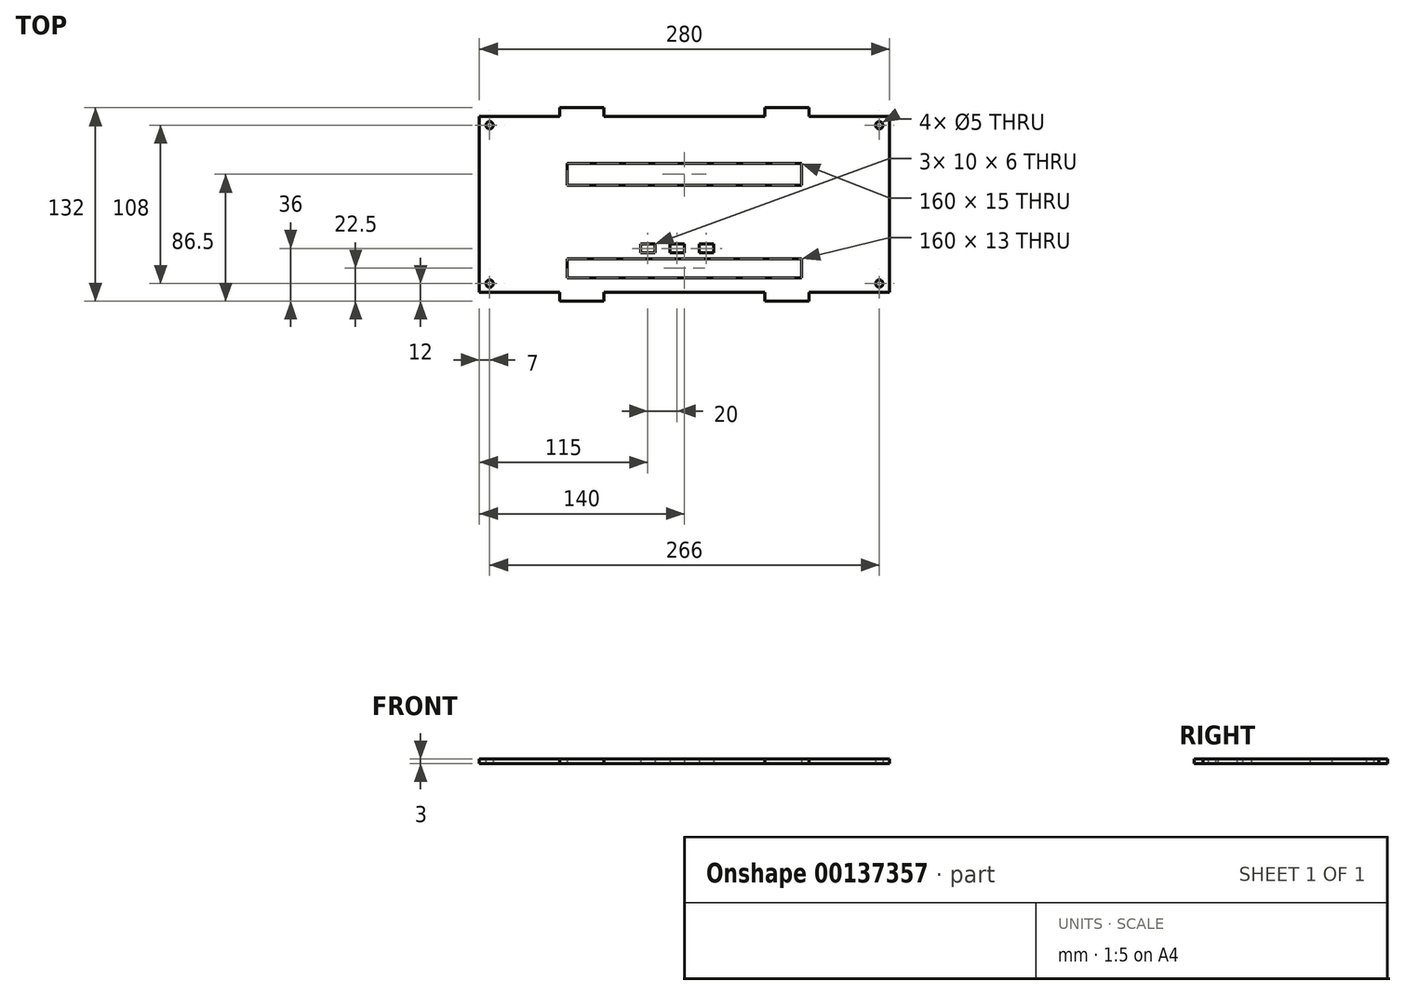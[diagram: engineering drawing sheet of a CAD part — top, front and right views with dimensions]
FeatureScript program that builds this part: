
annotation { "Feature Type Name" : "Feature", "Feature Type Description" : "" }
export const myFeature = defineFeature(function(context is Context, id is Id, definition is map)
    precondition{}
    {
        {
            var Q0;
            Q0=qCreatedBy(makeId("Top.planeOp"),FACE);
            var sketch = newSketch(context, id + "F0", { "sketchPlane" : qUnion([Q0])});
            skLineSegment(sketch, "E0.bottom", {"start": v(140, 60) * mm, "end": v(85, 60) * mm});
            skLineSegment(sketch, "E0.top", {"start": v(140, -60) * mm, "end": v(85, -60) * mm});
            skLineSegment(sketch, "E0.left", {"start": v(140, 60) * mm, "end": v(140, -60) * mm});
            skLineSegment(sketch, "E0.right", {"start": v(-140, 60) * mm, "end": v(-140, -60) * mm});
            skPoint(sketch, "E0.middle", {"position": v(0, 0) * mm});
            skLineSegment(sketch, "E1", {"start": v(-140, -60) * mm, "end": v(-133, -60) * mm, "construction": true});
            skLineSegment(sketch, "E2", {"start": v(-133, -60) * mm, "end": v(-133, -54) * mm, "construction": true});
            skCircle(sketch, "E3", {"center": v(-133, -54) * mm, "radius": 2.5 * mm});
            skCircle(sketch, "E4.MirrorC", {"center": v(-133, 54) * mm, "radius": 2.5 * mm});
            skCircle(sketch, "E5.MirrorC", {"center": v(133, 54) * mm, "radius": 2.5 * mm});
            skCircle(sketch, "E6.MirrorC", {"center": v(133, -54) * mm, "radius": 2.5 * mm});
            skLineSegment(sketch, "E7", {"start": v(0, -50) * mm, "end": v(-80, -50) * mm, "construction": true});
            skLineSegment(sketch, "E8.bottom", {"start": v(-80, -50) * mm, "end": v(80, -50) * mm});
            skLineSegment(sketch, "E8.top", {"start": v(-80, -37) * mm, "end": v(80, -37) * mm});
            skLineSegment(sketch, "E8.left", {"start": v(-80, -50) * mm, "end": v(-80, -37) * mm});
            skLineSegment(sketch, "E8.right", {"start": v(80, -50) * mm, "end": v(80, -37) * mm});
            skLineSegment(sketch, "E9", {"start": v(0, -37) * mm, "end": v(0, -32) * mm, "construction": true});
            skLineSegment(sketch, "E10", {"start": v(0, -32) * mm, "end": v(0, 13) * mm, "construction": true});
            skLineSegment(sketch, "E11", {"start": v(0, 13) * mm, "end": v(0, 28) * mm, "construction": true});
            skLineSegment(sketch, "E12", {"start": v(0, 13) * mm, "end": v(80, 13) * mm});
            skLineSegment(sketch, "E13", {"start": v(80, 13) * mm, "end": v(80, 23) * mm});
            skLineSegment(sketch, "E14", {"start": v(-80, 23) * mm, "end": v(-80, 13) * mm});
            skLineSegment(sketch, "E15", {"start": v(-80, 13) * mm, "end": v(0, 13) * mm});
            skLineSegment(sketch, "E16", {"start": v(0, 28) * mm, "end": v(0, 13) * mm, "construction": true});
            skLineSegment(sketch, "E17", {"start": v(0, 28) * mm, "end": v(0, 26) * mm, "construction": true});
            skLineSegment(sketch, "E18", {"start": v(0, 26) * mm, "end": v(0, 20) * mm, "construction": true});
            skLineSegment(sketch, "E19", {"start": v(0, 20) * mm, "end": v(0, 17) * mm, "construction": true});
            skLineSegment(sketch, "E20", {"start": v(-80, 23) * mm, "end": v(-80, 28) * mm});
            skLineSegment(sketch, "E21", {"start": v(-80, 28) * mm, "end": v(80, 28) * mm});
            skLineSegment(sketch, "E22", {"start": v(80, 28) * mm, "end": v(80, 23) * mm});
            skLineSegment(sketch, "E23", {"start": v(0, 13) * mm, "end": v(0, -27) * mm, "construction": true});
            skLineSegment(sketch, "E24", {"start": v(0, -27) * mm, "end": v(30, -27) * mm, "construction": true});
            skLineSegment(sketch, "E25", {"start": v(0, -27) * mm, "end": v(-30, -27) * mm, "construction": true});
            skLineSegment(sketch, "E26", {"start": v(-30, -27) * mm, "end": v(-30, -33) * mm});
            skLineSegment(sketch, "E27", {"start": v(-30, -33) * mm, "end": v(-20, -33) * mm});
            skLineSegment(sketch, "E28", {"start": v(-20, -33) * mm, "end": v(-20, -27) * mm});
            skLineSegment(sketch, "E29", {"start": v(-30, -27) * mm, "end": v(-20, -27) * mm});
            skLineSegment(sketch, "E30", {"start": v(-20, -27) * mm, "end": v(-10, -27) * mm, "construction": true});
            skLineSegment(sketch, "E31", {"start": v(-10, -27) * mm, "end": v(0, -27) * mm, "construction": true});
            skLineSegment(sketch, "E32", {"start": v(0, -27) * mm, "end": v(10, -27) * mm, "construction": true});
            skLineSegment(sketch, "E33", {"start": v(10, -27) * mm, "end": v(20, -27) * mm, "construction": true});
            skLineSegment(sketch, "E34", {"start": v(20, -27) * mm, "end": v(30, -27) * mm, "construction": true});
            skLineSegment(sketch, "E35", {"start": v(-10, -27) * mm, "end": v(-10, -33) * mm});
            skLineSegment(sketch, "E36", {"start": v(-10, -33) * mm, "end": v(0, -33) * mm});
            skLineSegment(sketch, "E37", {"start": v(0, -33) * mm, "end": v(0, -27) * mm});
            skLineSegment(sketch, "E38", {"start": v(-10, -27) * mm, "end": v(0, -27) * mm});
            skLineSegment(sketch, "E39.bottom", {"start": v(10, -27) * mm, "end": v(20, -27) * mm});
            skLineSegment(sketch, "E39.top", {"start": v(10, -33) * mm, "end": v(20, -33) * mm});
            skLineSegment(sketch, "E39.left", {"start": v(10, -27) * mm, "end": v(10, -33) * mm});
            skLineSegment(sketch, "E39.right", {"start": v(20, -27) * mm, "end": v(20, -33) * mm});
            skLineSegment(sketch, "E40", {"start": v(0, -60) * mm, "end": v(-55, -60) * mm, "construction": true});
            skLineSegment(sketch, "E41", {"start": v(-55, -60) * mm, "end": v(-55, -66) * mm});
            skLineSegment(sketch, "E42", {"start": v(-55, -66) * mm, "end": v(-85, -66) * mm});
            skLineSegment(sketch, "E43", {"start": v(-85, -66) * mm, "end": v(-85, -60) * mm});
            skLineSegment(sketch, "E44.trimOffspring", {"start": v(-85, -60) * mm, "end": v(-140, -60) * mm});
            skLineSegment(sketch, "E45", {"start": v(0, -60) * mm, "end": v(55, -60) * mm, "construction": true});
            skLineSegment(sketch, "E46", {"start": v(55, -60) * mm, "end": v(55, -66) * mm});
            skLineSegment(sketch, "E47", {"start": v(55, -66) * mm, "end": v(85, -66) * mm});
            skLineSegment(sketch, "E48", {"start": v(85, -66) * mm, "end": v(85, -60) * mm});
            skLineSegment(sketch, "E49.trimOffspring", {"start": v(55, -60) * mm, "end": v(-55, -60) * mm});
            skLineSegment(sketch, "E50", {"start": v(-140, 0) * mm, "end": v(140, 0) * mm, "construction": true});
            skLineSegment(sketch, "E51.MirrorCS", {"start": v(0, 60) * mm, "end": v(-55, 60) * mm, "construction": true});
            skLineSegment(sketch, "E52.MirrorCS", {"start": v(0, 60) * mm, "end": v(55, 60) * mm, "construction": true});
            skLineSegment(sketch, "E53", {"start": v(-55, 60) * mm, "end": v(-55, 66) * mm});
            skLineSegment(sketch, "E54", {"start": v(-55, 66) * mm, "end": v(-85, 66) * mm});
            skLineSegment(sketch, "E55", {"start": v(-85, 66) * mm, "end": v(-85, 60) * mm});
            skLineSegment(sketch, "E56", {"start": v(55, 60) * mm, "end": v(55, 66) * mm});
            skLineSegment(sketch, "E57", {"start": v(55, 66) * mm, "end": v(85, 66) * mm});
            skLineSegment(sketch, "E58", {"start": v(85, 66) * mm, "end": v(85, 60) * mm});
            skLineSegment(sketch, "E59.trimOffspring", {"start": v(55, 60) * mm, "end": v(-55, 60) * mm});
            skLineSegment(sketch, "E60.trimOffspring", {"start": v(-85, 60) * mm, "end": v(-140, 60) * mm});
            skSolve(sketch);
        }
        {
            var Q0;
            Q0=makeQuery(id+"F0.imprint","IMPRINT",FACE,{"disambiguationData":[TD([[makeQuery(id+"F0.imprint","IMPRINT",EDGE,{"derivedFrom":sQuery(id+"F0.wireOp",EDGE,"E0.bottom")}),1.0]])]});
            extrude(context, id + "F1", {"entities" : qUnion([Q0]), "endBound" : BoundingType.SYMMETRIC, "depth" : 3 * mm});
        }
    });
